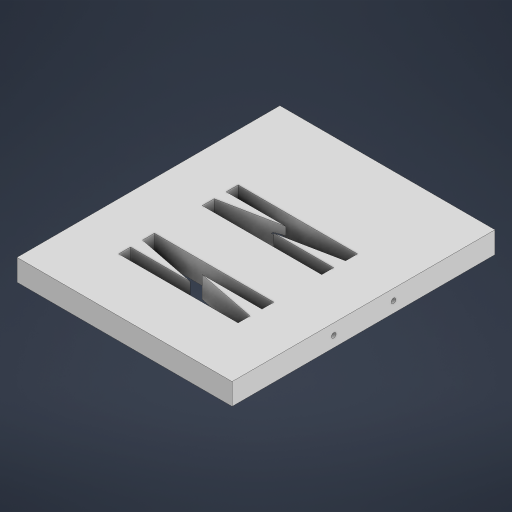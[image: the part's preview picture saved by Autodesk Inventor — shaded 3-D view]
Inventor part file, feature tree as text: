
AUTODESK INVENTOR PART (.ipt)
format: ipt  version: 2024 (Build 280153000, 153)  size: 217,600 bytes
history: native  units: mm
features: extrude x2, sketch x2, other x1
ambient origin geometry x8: Origin, YZ Plane, XZ Plane, XY Plane, X Axis, Y Axis, Z Axis, Center Point
bodies: Body1 (feature_tree)
feature tree (5):
  other  "Sólido1"
  extrude  "Extrusión1"  Depth=220.0mm
  extrude  "Extrusión2"  TaperAngle=0.0deg  [1 undecoded]
  sketch  "Boceto1"  dims[d0=180.0mm d1=220.0mm]
  sketch  "Boceto2"  dims[d2=90.0mm d3=0.0mm d5=10.0mm d6=40.0mm d7=10.0mm d8=10.0mm d9=100.0mm d11=45.0mm d13=10.0mm d14=10.0mm d15=10.0mm d16=75.0mm d17=18.0mm d18=0.0mm d20=4.0mm d23=4.0mm d24=50.0mm d25=85.0mm d26=500.0mm d27=0.0mm]
note: 1 required parameter value undecoded (feature->parameter linkage not recoverable at this tier; creation-order binding heuristic only, values carry confidence <= 0.55)
